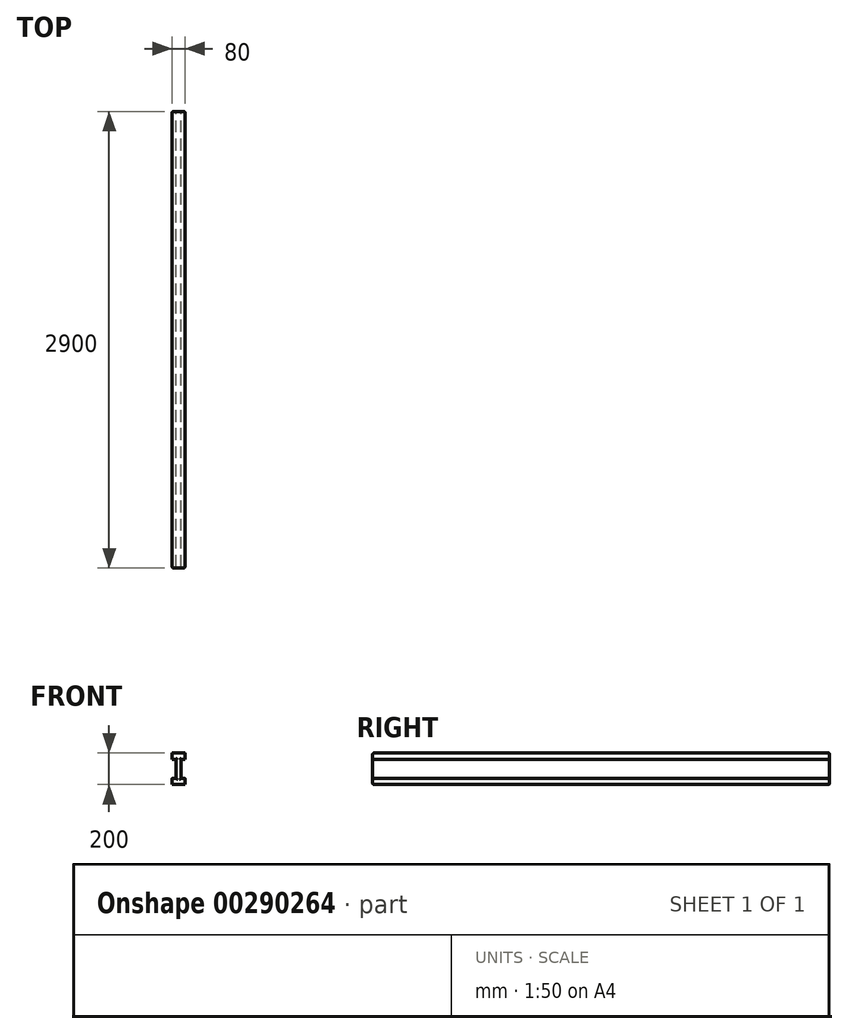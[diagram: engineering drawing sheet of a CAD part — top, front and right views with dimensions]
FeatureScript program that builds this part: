
annotation { "Feature Type Name" : "Feature", "Feature Type Description" : "" }
export const myFeature = defineFeature(function(context is Context, id is Id, definition is map)
    precondition{}
    {
        {
            var Q0;
            Q0=qCreatedBy(makeId("Front.planeOp"),FACE);
            var sketch = newSketch(context, id + "F0", { "sketchPlane" : qUnion([Q0])});
            skLineSegment(sketch, "E0", {"start": v(-43.52, 127.6) * mm, "end": v(36.48, 127.6) * mm});
            skLineSegment(sketch, "E1", {"start": v(36.48, 127.6) * mm, "end": v(36.48, 87.6) * mm});
            skLineSegment(sketch, "E2", {"start": v(36.48, 87.6) * mm, "end": v(11.48, 87.6) * mm});
            skLineSegment(sketch, "E3", {"start": v(11.48, 87.6) * mm, "end": v(11.48, -32.4) * mm});
            skLineSegment(sketch, "E4", {"start": v(11.48, -32.4) * mm, "end": v(36.48, -32.4) * mm});
            skLineSegment(sketch, "E5", {"start": v(36.48, -32.4) * mm, "end": v(36.48, -72.4) * mm});
            skLineSegment(sketch, "E6", {"start": v(36.48, -72.4) * mm, "end": v(-43.52, -72.4) * mm});
            skLineSegment(sketch, "E7", {"start": v(-43.52, -72.4) * mm, "end": v(-43.52, -32.4) * mm});
            skLineSegment(sketch, "E8", {"start": v(-43.52, -32.4) * mm, "end": v(-18.52, -32.4) * mm});
            skLineSegment(sketch, "E9", {"start": v(-18.52, -32.4) * mm, "end": v(-18.52, 87.6) * mm});
            skLineSegment(sketch, "E10", {"start": v(-18.52, 87.6) * mm, "end": v(-43.52, 87.6) * mm});
            skLineSegment(sketch, "E11", {"start": v(-43.52, 87.6) * mm, "end": v(-43.52, 127.6) * mm});
            skSolve(sketch);
        }
        {
            var Q0;
            Q0=makeQuery(id+"F0.imprint","IMPRINT",FACE,{"disambiguationData":[TD([[makeQuery(id+"F0.imprint","IMPRINT",EDGE,{"derivedFrom":sQuery(id+"F0.wireOp",EDGE,"E0")}),-1.0]])]});
            extrude(context, id + "F1", {"entities" : qUnion([Q0]), "depth" : 2900 * mm});
        }
        {
            var Q0;
            Q0=makeQuery(id+"F1.opExtrude","CAP_FACE",FACE,{"disambiguationData":[OSD([sQuery(id+"F0.wireOp",EDGE,"E0"),sQuery(id+"F0.wireOp",EDGE,"E1"),sQuery(id+"F0.wireOp",EDGE,"E2"),sQuery(id+"F0.wireOp",EDGE,"E3"),sQuery(id+"F0.wireOp",EDGE,"E4"),sQuery(id+"F0.wireOp",EDGE,"E5"),sQuery(id+"F0.wireOp",EDGE,"E6"),sQuery(id+"F0.wireOp",EDGE,"E7"),sQuery(id+"F0.wireOp",EDGE,"E8"),sQuery(id+"F0.wireOp",EDGE,"E9"),sQuery(id+"F0.wireOp",EDGE,"E10"),sQuery(id+"F0.wireOp",EDGE,"E11")])],"isStart":false});
            fillet(context, id + "F2", {"entities" : qUnion([Q0]), "radius" : 8 * mm, "tangentPropagation" : true, "allowEdgeOverflow" : false});
        }
        {
            var Q0;
            Q0=makeQuery(id+"F1.opExtrude","CAP_FACE",FACE,{"disambiguationData":[OSD([sQuery(id+"F0.wireOp",EDGE,"E0"),sQuery(id+"F0.wireOp",EDGE,"E1"),sQuery(id+"F0.wireOp",EDGE,"E2"),sQuery(id+"F0.wireOp",EDGE,"E3"),sQuery(id+"F0.wireOp",EDGE,"E4"),sQuery(id+"F0.wireOp",EDGE,"E5"),sQuery(id+"F0.wireOp",EDGE,"E6"),sQuery(id+"F0.wireOp",EDGE,"E7"),sQuery(id+"F0.wireOp",EDGE,"E8"),sQuery(id+"F0.wireOp",EDGE,"E9"),sQuery(id+"F0.wireOp",EDGE,"E10"),sQuery(id+"F0.wireOp",EDGE,"E11")])],"isStart":true});
            fillet(context, id + "F3", {"entities" : qUnion([Q0]), "radius" : 5 * mm, "tangentPropagation" : true, "allowEdgeOverflow" : false});
        }
    });
